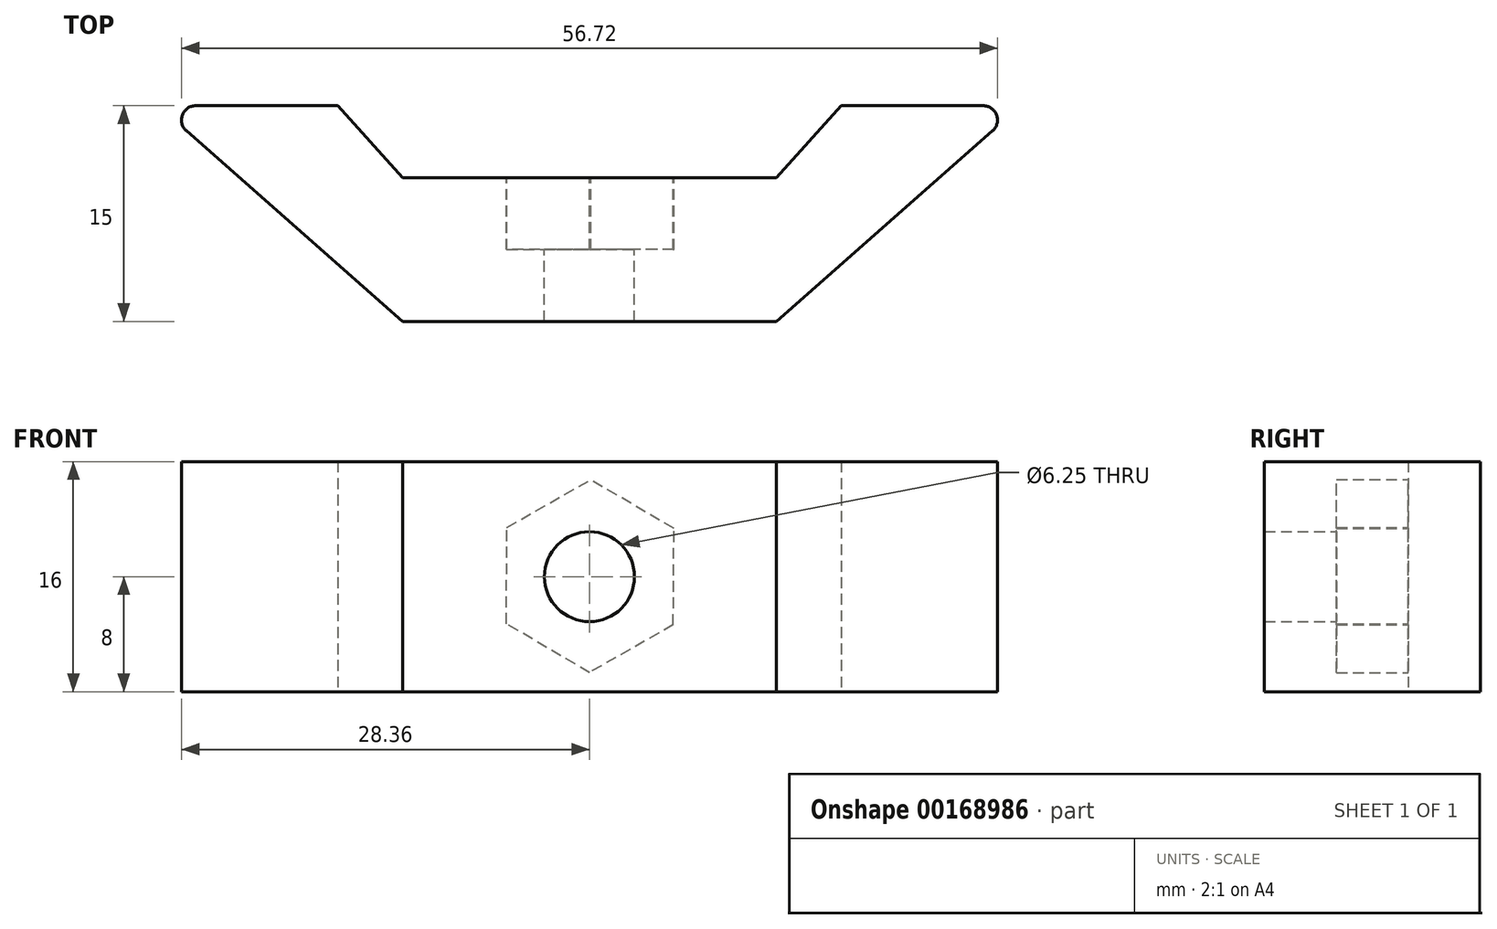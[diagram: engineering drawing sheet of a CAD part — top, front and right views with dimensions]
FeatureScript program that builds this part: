
annotation { "Feature Type Name" : "Feature", "Feature Type Description" : "" }
export const myFeature = defineFeature(function(context is Context, id is Id, definition is map)
    precondition{}
    {
        {
            var Q0;
            Q0=qCreatedBy(makeId("Top.planeOp"),FACE);
            var sketch = newSketch(context, id + "F0", { "sketchPlane" : qUnion([Q0])});
            skLineSegment(sketch, "E0", {"start": v(-30, 15) * mm, "end": v(-17.5, 15) * mm});
            skLineSegment(sketch, "E1", {"start": v(-17.5, 15) * mm, "end": v(-13, 10) * mm});
            skLineSegment(sketch, "E2", {"start": v(-13, 10) * mm, "end": v(0, 10) * mm});
            skLineSegment(sketch, "E3", {"start": v(0, 0) * mm, "end": v(-13, 0) * mm});
            skLineSegment(sketch, "E4", {"start": v(-13, 0) * mm, "end": v(-30, 15) * mm});
            skLineSegment(sketch, "E5.MirrorCS", {"start": v(13, 0) * mm, "end": v(30, 15) * mm});
            skLineSegment(sketch, "E6.MirrorCS", {"start": v(30, 15) * mm, "end": v(17.5, 15) * mm});
            skLineSegment(sketch, "E7.MirrorCS", {"start": v(17.5, 15) * mm, "end": v(13, 10) * mm});
            skLineSegment(sketch, "E8.MirrorCS", {"start": v(13, 10) * mm, "end": v(0, 10) * mm});
            skLineSegment(sketch, "E9.MirrorCS", {"start": v(0, 0) * mm, "end": v(13, 0) * mm});
            skSolve(sketch);
        }
        {
            var Q0;
            Q0=makeQuery(id+"F0.imprint","IMPRINT",FACE,{"disambiguationData":[TD([[makeQuery(id+"F0.imprint","IMPRINT",EDGE,{"derivedFrom":sQuery(id+"F0.wireOp",EDGE,"E0")}),-1.0]])]});
            extrude(context, id + "F1", {"entities" : qUnion([Q0]), "depth" : 16 * mm});
        }
        {
            var Q0;
            Q0=makeQuery(id+"F1.opExtrude","SWEPT_FACE",FACE,{"disambiguationData":[OSD([sQuery(id+"F0.wireOp",EDGE,"E2"),sQuery(id+"F0.wireOp",EDGE,"E8.MirrorCS")])]});
            var sketch = newSketch(context, id + "F2", { "sketchPlane" : qUnion([Q0])});
            skCircle(sketch, "E10", {"center": v(0, 8) * mm, "radius": 3.12 * mm});
            skPoint(sketch, "E10.centerSnap0", {"position": v(0, 38.55) * mm});
            skLineSegment(sketch, "E11", {"start": v(-5.82, 4.65) * mm, "end": v(-5.87, 11.35) * mm});
            skLineSegment(sketch, "E12", {"start": v(-5.87, 11.35) * mm, "end": v(-0.09, 14.74) * mm});
            skLineSegment(sketch, "E13", {"start": v(-5.82, 4.65) * mm, "end": v(0, 1.34) * mm});
            skLineSegment(sketch, "E14", {"start": v(0, 1.34) * mm, "end": v(5.78, 4.73) * mm});
            skLineSegment(sketch, "E15", {"start": v(5.78, 4.73) * mm, "end": v(5.74, 11.43) * mm});
            skLineSegment(sketch, "E16", {"start": v(5.74, 11.43) * mm, "end": v(-0.09, 14.74) * mm});
            skPoint(sketch, "E17", {"position": v(-5.85, 8) * mm});
            skSolve(sketch);
        }
        {
            var Q0;
            Q0=makeQuery(id+"F2.imprint","IMPRINT",FACE,{"disambiguationData":[TD([[makeQuery(id+"F2.imprint","IMPRINT",EDGE,{"derivedFrom":sQuery(id+"F2.wireOp",EDGE,"E10")}),1.0]])]});
            extrude(context, id + "F3", {"entities" : qUnion([Q0]), "operationType" : NewBodyOperationType.REMOVE, "endBound" : BoundingType.UP_TO_NEXT, "oppositeDirection" : true, "depth" : 25 * mm});
        }
        {
            var Q0;
            Q0=makeQuery(id+"F2.imprint","IMPRINT",FACE,{"disambiguationData":[TD([[makeQuery(id+"F2.imprint","IMPRINT",EDGE,{"derivedFrom":sQuery(id+"F2.wireOp",EDGE,"E10")}),-1.0]])]});
            extrude(context, id + "F4", {"entities" : qUnion([Q0]), "operationType" : NewBodyOperationType.REMOVE, "oppositeDirection" : true, "depth" : 5 * mm});
        }
        {
            var Q0;
            Q0=makeQuery(id+"F1.opExtrude","SWEPT_EDGE",EDGE,{"disambiguationData":[OSD([sQuery(id+"F0.wireOp",EDGE,"E5.MirrorCS"),sQuery(id+"F0.wireOp",EDGE,"E6.MirrorCS")])]});
            fillet(context, id + "F5", {"entities" : qUnion([Q0]), "radius" : 1 * mm, "tangentPropagation" : true, "allowEdgeOverflow" : false});
        }
        {
            var Q0;
            Q0=makeQuery(id+"F1.opExtrude","SWEPT_EDGE",EDGE,{"disambiguationData":[OSD([sQuery(id+"F0.wireOp",EDGE,"E0"),sQuery(id+"F0.wireOp",EDGE,"E4")])]});
            fillet(context, id + "F6", {"entities" : qUnion([Q0]), "radius" : 1 * mm, "tangentPropagation" : true, "allowEdgeOverflow" : false});
        }
    });
